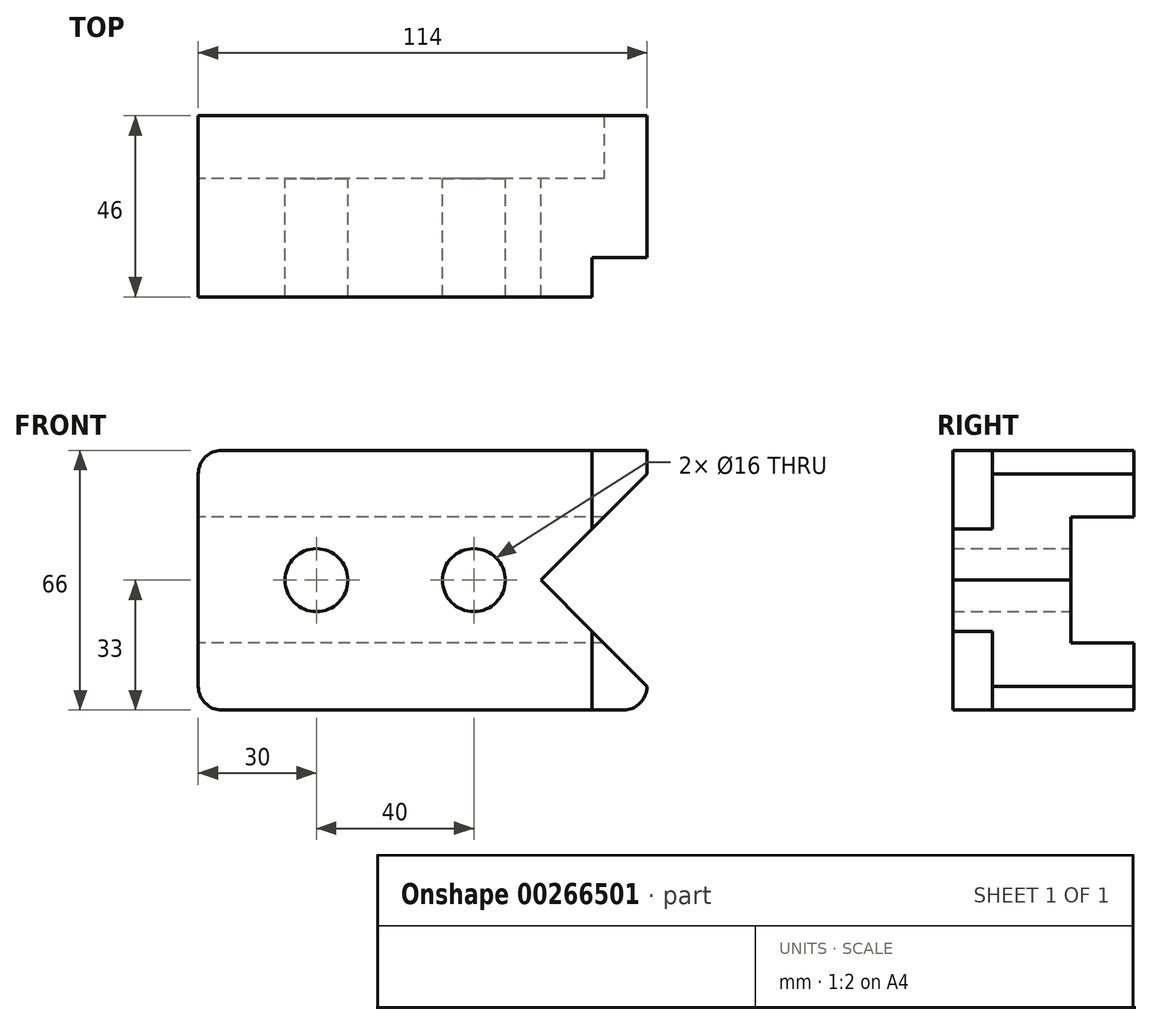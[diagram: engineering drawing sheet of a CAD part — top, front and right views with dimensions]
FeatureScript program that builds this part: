
annotation { "Feature Type Name" : "Feature", "Feature Type Description" : "" }
export const myFeature = defineFeature(function(context is Context, id is Id, definition is map)
    precondition{}
    {
        {
            var Q0;
            Q0=qCreatedBy(makeId("Front.planeOp"),FACE);
            var sketch = newSketch(context, id + "F0", { "sketchPlane" : qUnion([Q0])});
            skLineSegment(sketch, "E0", {"start": v(0, 0) * mm, "end": v(114, 0) * mm});
            skLineSegment(sketch, "E1", {"start": v(114, 0) * mm, "end": v(114, 66) * mm});
            skLineSegment(sketch, "E2", {"start": v(114, 66) * mm, "end": v(0, 66) * mm});
            skLineSegment(sketch, "E3", {"start": v(0, 66) * mm, "end": v(0, 0) * mm});
            skLineSegment(sketch, "E4", {"start": v(0, 0) * mm, "end": v(0, 33) * mm});
            skLineSegment(sketch, "E5", {"start": v(0, 33) * mm, "end": v(114, 33) * mm});
            skLineSegment(sketch, "E6", {"start": v(114, 33) * mm, "end": v(87, 33) * mm});
            skLineSegment(sketch, "E7", {"start": v(87, 33) * mm, "end": v(114, 60) * mm});
            skLineSegment(sketch, "E8", {"start": v(87, 33) * mm, "end": v(114, 6) * mm});
            skSolve(sketch);
        }
        {
            var Q0;
            {var subQ0=sQuery(id+"F0.wireOp",EDGE,"E2");Q0=makeQuery(id+"F0.imprint","IMPRINT",FACE,{"disambiguationData":[TD([[makeQuery(id+"F0.imprint","IMPRINT",EDGE,{"derivedFrom":subQ0}),1.0]])]});}
            var Q1;
            {var subQ1=sQuery(id+"F0.wireOp",EDGE,"E0");Q1=makeQuery(id+"F0.imprint","IMPRINT",FACE,{"disambiguationData":[TD([[makeQuery(id+"F0.imprint","IMPRINT",EDGE,{"derivedFrom":subQ1}),1.0]])]});}
            extrude(context, id + "F1", {"entities" : qUnion([Q0, Q1]), "depth" : 46 * mm});
        }
        {
            var Q0;
            Q0=makeQuery(id+"F1.opExtrude","SWEPT_FACE",FACE,{"disambiguationData":[OSD([sQuery(id+"F0.wireOp",EDGE,"E2")])]});
            var sketch = newSketch(context, id + "F2", { "sketchPlane" : qUnion([Q0])});
            skLineSegment(sketch, "E9.bottom", {"start": v(114, -46) * mm, "end": v(100, -46) * mm});
            skLineSegment(sketch, "E9.top", {"start": v(114, -36) * mm, "end": v(100, -36) * mm});
            skLineSegment(sketch, "E9.left", {"start": v(114, -46) * mm, "end": v(114, -36) * mm});
            skLineSegment(sketch, "E9.right", {"start": v(100, -46) * mm, "end": v(100, -36) * mm});
            skSolve(sketch);
        }
        {
            var Q0;
            Q0=makeQuery(id+"F2.imprint","IMPRINT",FACE,{"disambiguationData":[TD([[makeQuery(id+"F2.imprint","IMPRINT",EDGE,{"derivedFrom":sQuery(id+"F2.wireOp",EDGE,"E9.bottom")}),-1.0]])]});
            extrude(context, id + "F3", {"entities" : qUnion([Q0]), "operationType" : NewBodyOperationType.REMOVE, "endBound" : BoundingType.THROUGH_ALL, "oppositeDirection" : true, "depth" : 25 * mm});
        }
        {
            var Q0;
            Q0=makeQuery(id+"F1.opExtrude","SWEPT_FACE",FACE,{"disambiguationData":[OSD([sQuery(id+"F0.wireOp",EDGE,"E3"),sQuery(id+"F0.wireOp",EDGE,"E4")])]});
            var sketch = newSketch(context, id + "F4", { "sketchPlane" : qUnion([Q0])});
            skLineSegment(sketch, "E10.bottom", {"start": v(0, 49) * mm, "end": v(16, 49) * mm});
            skLineSegment(sketch, "E10.top", {"start": v(0, 17) * mm, "end": v(16, 17) * mm});
            skLineSegment(sketch, "E10.left", {"start": v(0, 49) * mm, "end": v(0, 17) * mm});
            skLineSegment(sketch, "E10.right", {"start": v(16, 49) * mm, "end": v(16, 17) * mm});
            skSolve(sketch);
        }
        {
            var Q0;
            Q0=makeQuery(id+"F4.imprint","IMPRINT",FACE,{"disambiguationData":[TD([[makeQuery(id+"F4.imprint","IMPRINT",EDGE,{"derivedFrom":sQuery(id+"F4.wireOp",EDGE,"E10.bottom")}),-1.0]])]});
            extrude(context, id + "F5", {"entities" : qUnion([Q0]), "operationType" : NewBodyOperationType.REMOVE, "endBound" : BoundingType.THROUGH_ALL, "oppositeDirection" : true, "depth" : 25 * mm});
        }
        {
            var Q0;
            Q0=qCreatedBy(makeId("Front.planeOp"),FACE);
            var sketch = newSketch(context, id + "F6", { "sketchPlane" : qUnion([Q0])});
            skCircle(sketch, "E11", {"center": v(30, 33) * mm, "radius": 8 * mm});
            skCircle(sketch, "E12", {"center": v(70, 33) * mm, "radius": 8 * mm});
            skSolve(sketch);
        }
        {
            var Q0;
            Q0 = qSketchRegion(id + "F6", true);
            extrude(context, id + "F7", {"entities" : qUnion([Q0]), "operationType" : NewBodyOperationType.ADD, "depth" : 25 * mm});
        }
        {
            var Q0;
            Q0=makeQuery(id+"F6.imprint","IMPRINT",FACE,{"disambiguationData":[TD([[makeQuery(id+"F6.imprint","IMPRINT",EDGE,{"derivedFrom":sQuery(id+"F6.wireOp",EDGE,"E11")}),1.0]])]});
            var Q1;
            Q1=makeQuery(id+"F6.imprint","IMPRINT",FACE,{"disambiguationData":[TD([[makeQuery(id+"F6.imprint","IMPRINT",EDGE,{"derivedFrom":sQuery(id+"F6.wireOp",EDGE,"E12")}),1.0]])]});
            extrude(context, id + "F8", {"entities" : qUnion([Q0, Q1]), "operationType" : NewBodyOperationType.REMOVE, "endBound" : BoundingType.THROUGH_ALL, "depth" : 25 * mm});
        }
        {
            var Q0;
            Q0=makeQuery(id+"F1.opExtrude","SWEPT_EDGE",EDGE,{"disambiguationData":[OSD([sQuery(id+"F0.wireOp",EDGE,"E2"),sQuery(id+"F0.wireOp",EDGE,"E3")])]});
            var Q1;
            Q1=makeQuery(id+"F1.opExtrude","SWEPT_EDGE",EDGE,{"disambiguationData":[OSD([sQuery(id+"F0.wireOp",EDGE,"E0"),sQuery(id+"F0.wireOp",EDGE,"E4")])]});
            fillet(context, id + "F9", {"entities" : qUnion([Q0, Q1]), "radius" : 6 * mm, "tangentPropagation" : true, "allowEdgeOverflow" : false});
        }
    });
